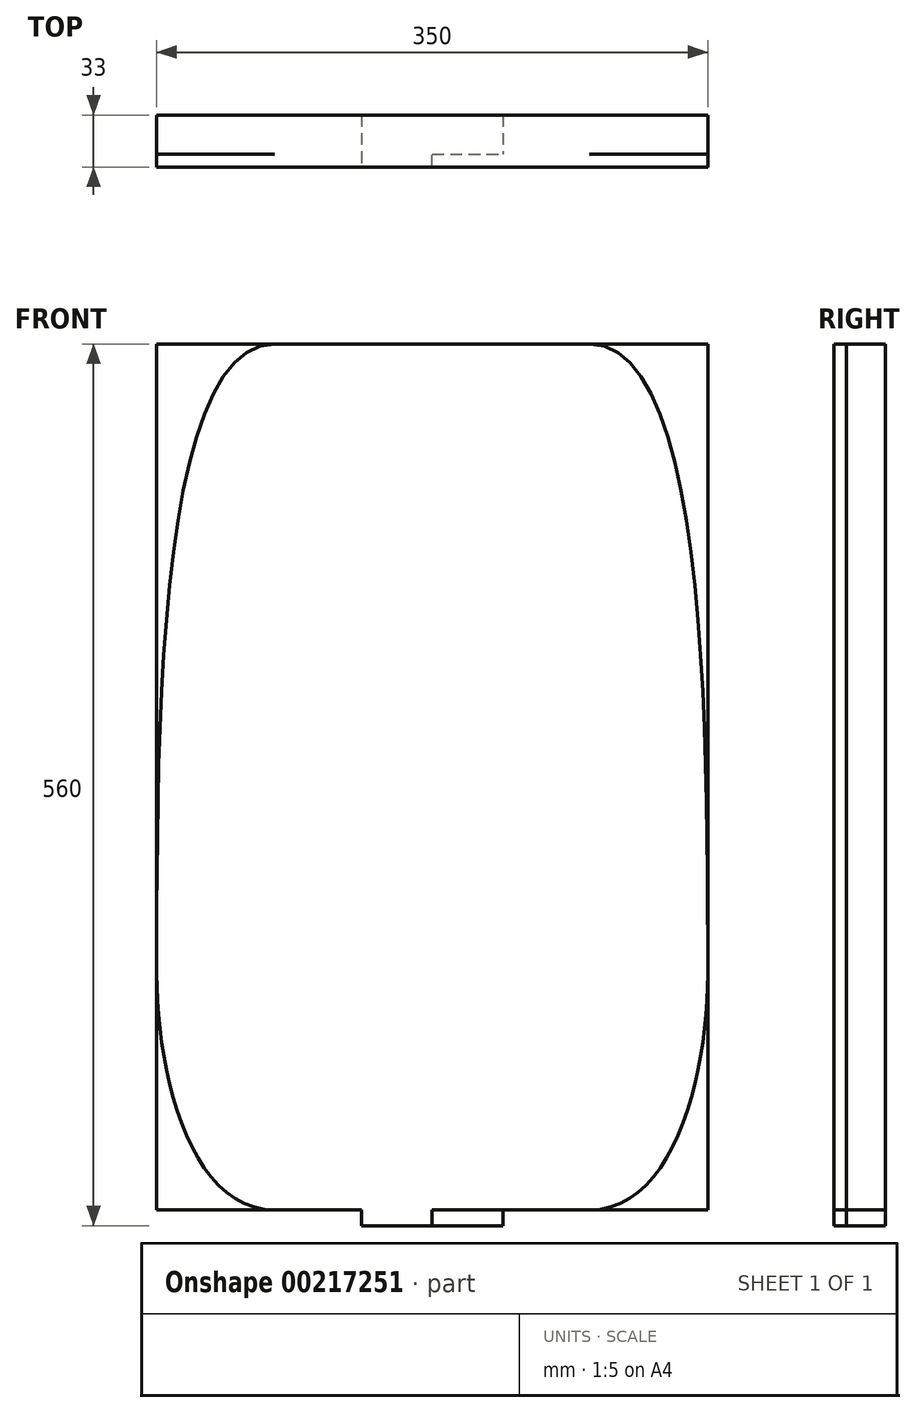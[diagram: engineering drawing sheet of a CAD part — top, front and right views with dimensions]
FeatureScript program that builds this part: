
annotation { "Feature Type Name" : "Feature", "Feature Type Description" : "" }
export const myFeature = defineFeature(function(context is Context, id is Id, definition is map)
    precondition{}
    {
        {
            var Q0;
            Q0=qCreatedBy(makeId("Front.planeOp"),FACE);
            var sketch = newSketch(context, id + "F0", { "sketchPlane" : qUnion([Q0])});
            skLineSegment(sketch, "E0.bottom", {"start": v(-175, 275) * mm, "end": v(175, 275) * mm});
            skLineSegment(sketch, "E0.top", {"start": v(-175, -275) * mm, "end": v(175, -275) * mm});
            skLineSegment(sketch, "E0.right", {"start": v(175, 275) * mm, "end": v(175, -275) * mm});
            skPoint(sketch, "E0.middle", {"position": v(0, 0) * mm});
            skFitSpline(sketch, "E1", {"points": [v(-100, 275) * mm, v(-175, -125) * mm], "startDerivative": vector(-225, 0) * mm, "endDerivative": vector(0, -458.8) * mm});
            skFitSpline(sketch, "E2", {"points": [v(-100, -275) * mm, v(-175, -125) * mm], "startDerivative": vector(-161.54, 0) * mm, "endDerivative": vector(0, 190.04) * mm});
            skFitSpline(sketch, "E3.MirrorCS", {"points": [v(100, 275) * mm, v(175, -125) * mm], "startDerivative": vector(225, 0) * mm, "endDerivative": vector(0, -458.8) * mm});
            skFitSpline(sketch, "E4.MirrorCS", {"points": [v(100, -275) * mm, v(175, -125) * mm], "startDerivative": vector(161.54, 0) * mm, "endDerivative": vector(0, 190.04) * mm});
            skLineSegment(sketch, "E5", {"start": v(-175, 275) * mm, "end": v(-175, -275) * mm});
            skPoint(sketch, "E6", {"position": v(0, -275) * mm});
            skLineSegment(sketch, "E7", {"start": v(-45, -285) * mm, "end": v(-45, -275) * mm});
            skLineSegment(sketch, "E8", {"start": v(45, -285) * mm, "end": v(45, -275) * mm});
            skLineSegment(sketch, "E9", {"start": v(-45, -285) * mm, "end": v(45, -285) * mm});
            skLineSegment(sketch, "E10", {"start": v(0, -275) * mm, "end": v(0, -285) * mm});
            skSolve(sketch);
        }
        {
            var Q0;
            Q0 = qSketchRegion(id + "F0", true);
            extrude(context, id + "F1", {"entities" : qUnion([Q0]), "oppositeDirection" : true, "depth" : 25 * mm});
        }
        {
            var Q0;
            {var subQ1=sQuery(id+"F0.wireOp",EDGE,"E1");Q0=makeQuery(id+"F0.imprint","IMPRINT",FACE,{"disambiguationData":[TD([[makeQuery(id+"F0.imprint","IMPRINT",EDGE,{"derivedFrom":subQ1}),1.0]])]});}
            var Q1;
            {var subQ0=sQuery(id+"F0.wireOp",EDGE,"E7");Q1=makeQuery(id+"F0.imprint","IMPRINT",FACE,{"disambiguationData":[TD([[makeQuery(id+"F0.imprint","IMPRINT",EDGE,{"derivedFrom":subQ0}),-1.0]])]});}
            extrude(context, id + "F2", {"entities" : qUnion([Q0, Q1]), "operationType" : NewBodyOperationType.ADD, "depth" : 8 * mm});
        }
    });
